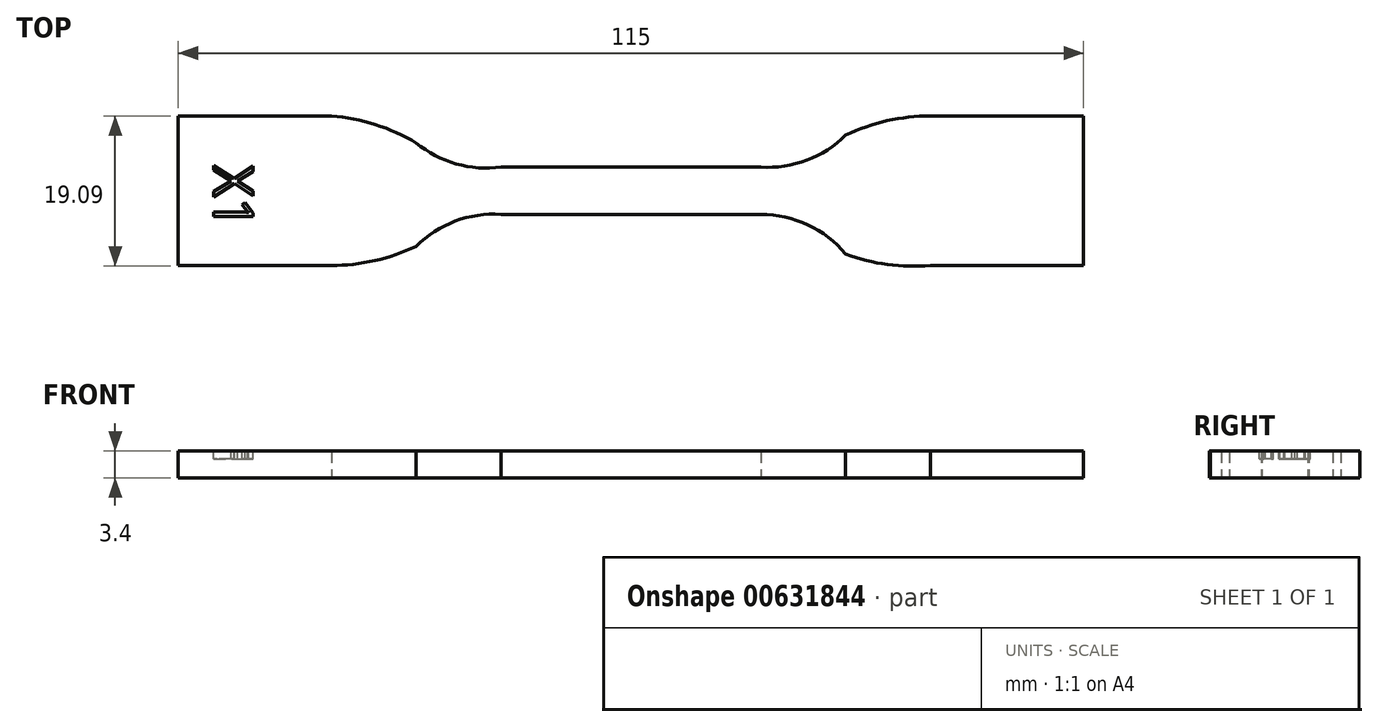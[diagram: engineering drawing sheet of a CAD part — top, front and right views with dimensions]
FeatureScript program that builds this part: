
annotation { "Feature Type Name" : "Feature", "Feature Type Description" : "" }
export const myFeature = defineFeature(function(context is Context, id is Id, definition is map)
    precondition{}
    {
        {
            var Q0;
            Q0=qCreatedBy(makeId("Top.planeOp"),FACE);
            var sketch = newSketch(context, id + "F0", { "sketchPlane" : qUnion([Q0])});
            skLineSegment(sketch, "E0", {"start": v(-33.87, 19.78) * mm, "end": v(-33.87, 0.78) * mm});
            skLineSegment(sketch, "E1", {"start": v(-33.87, 0.78) * mm, "end": v(-14.43, 0.78) * mm});
            skLineSegment(sketch, "E2", {"start": v(-33.87, 19.78) * mm, "end": v(-14.43, 19.78) * mm});
            skLineSegment(sketch, "E3", {"start": v(61.69, 19.78) * mm, "end": v(81.13, 19.78) * mm});
            skLineSegment(sketch, "E4", {"start": v(81.13, 19.78) * mm, "end": v(81.13, 0.78) * mm});
            skLineSegment(sketch, "E5", {"start": v(81.13, 0.78) * mm, "end": v(61.69, 0.78) * mm});
            skLineSegment(sketch, "E6", {"start": v(7.13, 13.28) * mm, "end": v(40.13, 13.28) * mm});
            skLineSegment(sketch, "E7", {"start": v(7.13, 7.28) * mm, "end": v(40.13, 7.28) * mm});
            skArc(sketch, "E8", {"start": v(-3.65, 16.36) * mm, "mid": v(-8.85, 18.69) * mm, "end": v(-14.43, 19.78) * mm});
            skArc(sketch, "E9", {"start": v(-3.65, 16.36) * mm, "mid": v(1.42, 13.7) * mm, "end": v(7.13, 13.28) * mm});
            skArc(sketch, "E10", {"start": v(-14.43, 0.78) * mm, "mid": v(-8.9, 1.4) * mm, "end": v(-3.65, 3.22) * mm});
            skArc(sketch, "E11", {"start": v(7.13, 7.28) * mm, "mid": v(1.3, 6.41) * mm, "end": v(-3.65, 3.22) * mm});
            skArc(sketch, "E12", {"start": v(40.13, 13.28) * mm, "mid": v(45.95, 14.15) * mm, "end": v(50.9, 17.34) * mm});
            skArc(sketch, "E13", {"start": v(61.69, 19.78) * mm, "mid": v(56.16, 19.16) * mm, "end": v(50.9, 17.34) * mm});
            skArc(sketch, "E14", {"start": v(50.9, 2.21) * mm, "mid": v(46.08, 5.95) * mm, "end": v(40.13, 7.28) * mm});
            skArc(sketch, "E15", {"start": v(50.9, 2.21) * mm, "mid": v(56.22, 0.9) * mm, "end": v(61.69, 0.78) * mm});
            skSolve(sketch);
        }
        {
            var Q0;
            Q0=qSketchRegion(id+"F0",true);
            extrude(context, id + "F1", {"entities" : qUnion([Q0]), "depth" : 3.4 * mm, "offsetDistance" : 25 * mm});
        }
        {
            var Q0;
            Q0=makeQuery(id+"F1.opExtrude","CAP_FACE",FACE,{"disambiguationData":[OSD([sQuery(id+"F0.wireOp",EDGE,"E0"),sQuery(id+"F0.wireOp",EDGE,"E1"),sQuery(id+"F0.wireOp",EDGE,"E2"),sQuery(id+"F0.wireOp",EDGE,"E3"),sQuery(id+"F0.wireOp",EDGE,"E4"),sQuery(id+"F0.wireOp",EDGE,"E5"),sQuery(id+"F0.wireOp",EDGE,"E6"),sQuery(id+"F0.wireOp",EDGE,"E7"),sQuery(id+"F0.wireOp",EDGE,"E8"),sQuery(id+"F0.wireOp",EDGE,"E9"),sQuery(id+"F0.wireOp",EDGE,"E10"),sQuery(id+"F0.wireOp",EDGE,"E11"),sQuery(id+"F0.wireOp",EDGE,"E12"),sQuery(id+"F0.wireOp",EDGE,"E13"),sQuery(id+"F0.wireOp",EDGE,"E14"),sQuery(id+"F0.wireOp",EDGE,"E15")])],"isStart":false});
            var sketch = newSketch(context, id + "F2", { "sketchPlane" : qUnion([Q0])});
            skText(sketch, "E16", { "text": "X1", "fontName": "OpenSans-Regular.ttf"});
            const initialGuessF2  = {"E16": [-0.02939, 0.01353, 0, -1, 0.00508]};
            skSetInitialGuess(sketch, initialGuessF2);
            skSolve(sketch);
        }
        {
            var Q0;
            Q0=qSketchRegion(id+"F2",true);
            extrude(context, id + "F3", {"entities" : qUnion([Q0]), "operationType" : NewBodyOperationType.REMOVE, "oppositeDirection" : true, "depth" : 1 * mm, "offsetDistance" : 25 * mm});
        }
    });
